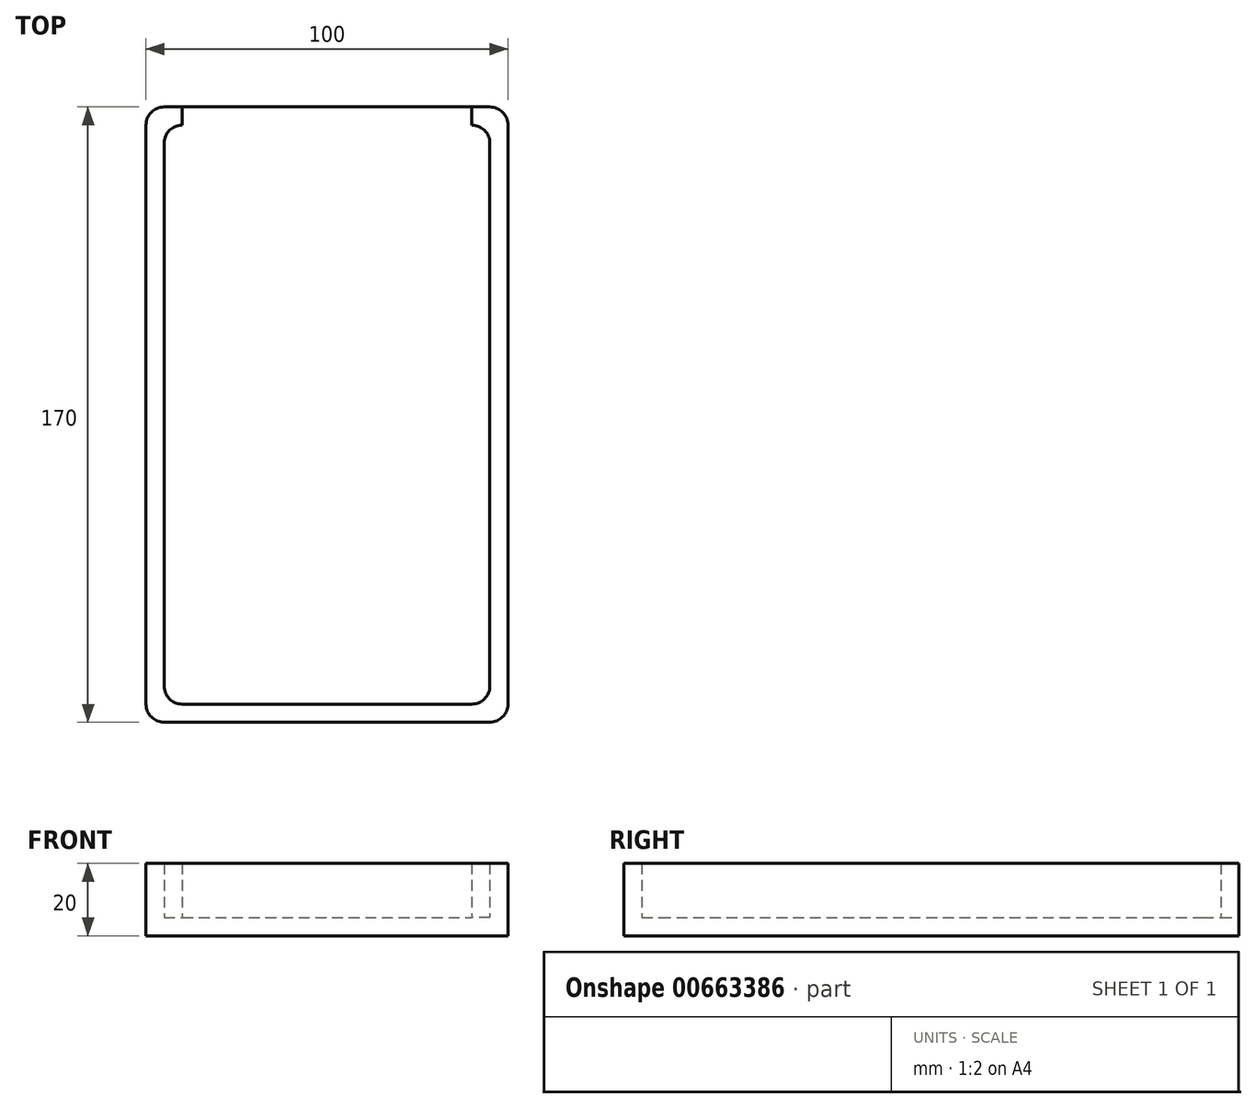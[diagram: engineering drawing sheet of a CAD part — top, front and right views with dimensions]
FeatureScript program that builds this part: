
annotation { "Feature Type Name" : "Feature", "Feature Type Description" : "" }
export const myFeature = defineFeature(function(context is Context, id is Id, definition is map)
    precondition{}
    {
        {
            var Q0;
            Q0=qCreatedBy(makeId("Top.planeOp"),FACE);
            var sketch = newSketch(context, id + "F0", { "sketchPlane" : qUnion([Q0])});
            skLineSegment(sketch, "E0.bottom", {"start": v(-45, -85) * mm, "end": v(45, -85) * mm});
            skLineSegment(sketch, "E0.top", {"start": v(-45, 85) * mm, "end": v(45, 85) * mm});
            skLineSegment(sketch, "E0.left", {"start": v(-50, -80) * mm, "end": v(-50, 80) * mm});
            skLineSegment(sketch, "E0.right", {"start": v(50, -80) * mm, "end": v(50, 80) * mm});
            skPoint(sketch, "E0.middle", {"position": v(0, 0) * mm});
            skLineSegment(sketch, "E1.bottom", {"start": v(-40, -80) * mm, "end": v(40, -80) * mm});
            skLineSegment(sketch, "E1.top", {"start": v(-40, 80) * mm, "end": v(40, 80) * mm});
            skLineSegment(sketch, "E1.left", {"start": v(-45, -75) * mm, "end": v(-45, 75) * mm});
            skLineSegment(sketch, "E1.right", {"start": v(45, -75) * mm, "end": v(45, 75) * mm});
            skPoint(sketch, "E2.visualSharp", {"position": v(-45, -80) * mm});
            skArc(sketch, "E2.filletArc", {"start": v(-45, -75) * mm, "mid": v(-43.54, -78.54) * mm, "end": v(-40, -80) * mm});
            skPoint(sketch, "E3.visualSharp", {"position": v(-50, -85) * mm});
            skArc(sketch, "E3.filletArc", {"start": v(-50, -80) * mm, "mid": v(-48.54, -83.54) * mm, "end": v(-45, -85) * mm});
            skPoint(sketch, "E4.visualSharp", {"position": v(50, -85) * mm});
            skArc(sketch, "E4.filletArc", {"start": v(45, -85) * mm, "mid": v(48.54, -83.54) * mm, "end": v(50, -80) * mm});
            skArc(sketch, "E5.filletArc", {"start": v(40, -80) * mm, "mid": v(43.54, -78.54) * mm, "end": v(45, -75) * mm});
            skPoint(sketch, "E6.visualSharp", {"position": v(-45, 80) * mm});
            skArc(sketch, "E6.filletArc", {"start": v(-40, 80) * mm, "mid": v(-43.54, 78.54) * mm, "end": v(-45, 75) * mm});
            skPoint(sketch, "E7.visualSharp", {"position": v(-50, 85) * mm});
            skArc(sketch, "E7.filletArc", {"start": v(-45, 85) * mm, "mid": v(-48.54, 83.54) * mm, "end": v(-50, 80) * mm});
            skPoint(sketch, "E8.visualSharp", {"position": v(45, 80) * mm});
            skArc(sketch, "E8.filletArc", {"start": v(45, 75) * mm, "mid": v(43.54, 78.54) * mm, "end": v(40, 80) * mm});
            skPoint(sketch, "E9.visualSharp", {"position": v(50, 85) * mm});
            skArc(sketch, "E9.filletArc", {"start": v(50, 80) * mm, "mid": v(48.54, 83.54) * mm, "end": v(45, 85) * mm});
            skLineSegment(sketch, "E10", {"start": v(-40, 80) * mm, "end": v(-40, 85) * mm});
            skLineSegment(sketch, "E11", {"start": v(40, 80) * mm, "end": v(40, 85) * mm});
            skSolve(sketch);
        }
        {
            var Q0;
            Q0=makeQuery(id+"F0.imprint","IMPRINT",FACE,{"disambiguationData":[TD([[makeQuery(id+"F0.imprint","IMPRINT",EDGE,{"derivedFrom":sQuery(id+"F0.wireOp",EDGE,"E0.bottom")}),1.0]])]});
            extrude(context, id + "F1", {"entities" : qUnion([Q0]), "depth" : 20 * mm, "offsetDistance" : 25 * mm});
        }
        {
            var Q0;
            Q0=makeQuery(id+"F0.imprint","IMPRINT",FACE,{"disambiguationData":[TD([[makeQuery(id+"F0.imprint","IMPRINT",EDGE,{"derivedFrom":sQuery(id+"F0.wireOp",EDGE,"E1.bottom")}),1.0]])]});
            var Q1;
            Q1=makeQuery(id+"F0.imprint","IMPRINT",FACE,{"disambiguationData":[TD([[makeQuery(id+"F0.imprint","IMPRINT",EDGE,{"derivedFrom":sQuery(id+"F0.wireOp",EDGE,"E1.top")}),1.0]])]});
            extrude(context, id + "F2", {"entities" : qUnion([Q0, Q1]), "operationType" : NewBodyOperationType.ADD, "depth" : 5 * mm, "offsetDistance" : 25 * mm});
        }
    });
